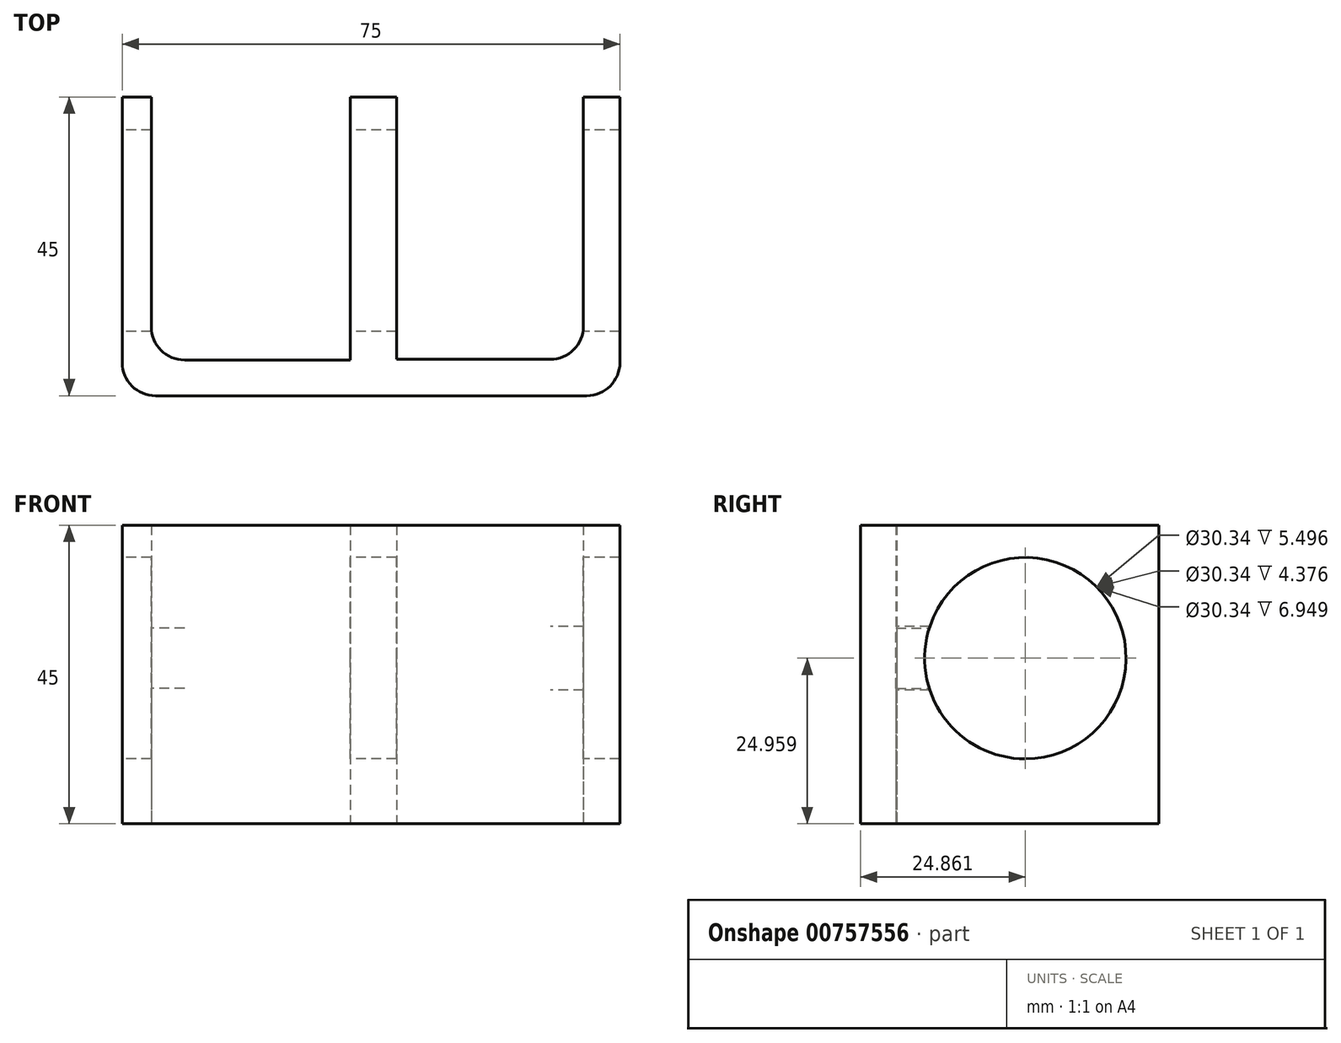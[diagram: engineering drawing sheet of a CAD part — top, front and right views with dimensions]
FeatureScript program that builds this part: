
annotation { "Feature Type Name" : "Feature", "Feature Type Description" : "" }
export const myFeature = defineFeature(function(context is Context, id is Id, definition is map)
    precondition{}
    {
        {
            var Q0;
            Q0=qCreatedBy(makeId("Top.planeOp"),FACE);
            var sketch = newSketch(context, id + "F0", { "sketchPlane" : qUnion([Q0])});
            skLineSegment(sketch, "E0.bottom", {"start": v(-37.5, 22.5) * mm, "end": v(37.5, 22.5) * mm});
            skLineSegment(sketch, "E0.top", {"start": v(-37.5, -22.5) * mm, "end": v(37.5, -22.5) * mm});
            skLineSegment(sketch, "E0.left", {"start": v(-37.5, 22.5) * mm, "end": v(-37.5, -22.5) * mm});
            skLineSegment(sketch, "E0.right", {"start": v(37.5, 22.5) * mm, "end": v(37.5, -22.5) * mm});
            skPoint(sketch, "E0.middle", {"position": v(0, 0) * mm});
            skLineSegment(sketch, "E1.bottom", {"start": v(-33.12, 24.35) * mm, "end": v(-3.12, 24.35) * mm});
            skLineSegment(sketch, "E1.top", {"start": v(-33.12, -17.11) * mm, "end": v(-3.12, -17.11) * mm});
            skLineSegment(sketch, "E1.left", {"start": v(-33.12, 24.35) * mm, "end": v(-33.12, -17.11) * mm});
            skLineSegment(sketch, "E1.right", {"start": v(-3.12, 24.35) * mm, "end": v(-3.12, -17.11) * mm});
            skLineSegment(sketch, "E2.bottom", {"start": v(3.83, 24.91) * mm, "end": v(32, 24.91) * mm});
            skLineSegment(sketch, "E2.top", {"start": v(3.83, -17.03) * mm, "end": v(32, -17.03) * mm});
            skLineSegment(sketch, "E2.left", {"start": v(3.83, 24.91) * mm, "end": v(3.83, -17.03) * mm});
            skLineSegment(sketch, "E2.right", {"start": v(32, 24.91) * mm, "end": v(32, -17.03) * mm});
            skSolve(sketch);
        }
        {
            var Q0;
            Q0=makeQuery(id+"F0.imprint","IMPRINT",FACE,{"disambiguationData":[TD([[makeQuery(id+"F0.imprint","IMPRINT",EDGE,{"derivedFrom":sQuery(id+"F0.wireOp",EDGE,"E0.top")}),1.0]])]});
            extrude(context, id + "F1", {"entities" : qUnion([Q0]), "depth" : 45 * mm, "offsetDistance" : 25 * mm});
        }
        {
            var Q0;
            Q0=makeQuery(id+"F1.opExtrude","SWEPT_EDGE",EDGE,{"disambiguationData":[OSD([sQuery(id+"F0.wireOp",EDGE,"E0.top"),sQuery(id+"F0.wireOp",EDGE,"E0.right")])]});
            var Q1;
            Q1=makeQuery(id+"F1.opExtrude","SWEPT_EDGE",EDGE,{"disambiguationData":[OSD([sQuery(id+"F0.wireOp",EDGE,"E0.top"),sQuery(id+"F0.wireOp",EDGE,"E0.left")])]});
            fillet(context, id + "F2", {"entities" : qUnion([Q0, Q1]), "radius" : 5 * mm, "tangentPropagation" : true, "allowEdgeOverflow" : false});
        }
        {
            var Q0;
            Q0=makeQuery(id+"F1.opExtrude","SWEPT_FACE",FACE,{"disambiguationData":[OSD([sQuery(id+"F0.wireOp",EDGE,"E0.left")])]});
            var sketch = newSketch(context, id + "F3", { "sketchPlane" : qUnion([Q0])});
            skCircle(sketch, "E3", {"center": v(-2.36, 24.96) * mm, "radius": 15.17 * mm});
            skPoint(sketch, "E3.first.point", {"position": v(-14.4, 34.19) * mm});
            skPoint(sketch, "E3.second.point", {"position": v(-10.1, 38) * mm});
            skPoint(sketch, "E3.third.point", {"position": v(-1.66, 40.11) * mm});
            skSolve(sketch);
        }
        {
            var Q0;
            Q0=makeQuery(id+"F3.imprint","IMPRINT",FACE,{"disambiguationData":[TD([[makeQuery(id+"F3.imprint","IMPRINT",EDGE,{"derivedFrom":sQuery(id+"F3.wireOp",EDGE,"E3")}),1.0]])]});
            extrude(context, id + "F4", {"entities" : qUnion([Q0]), "operationType" : NewBodyOperationType.REMOVE, "oppositeDirection" : true, "depth" : 100 * mm, "offsetDistance" : 25 * mm});
        }
        {
            var Q0;
            Q0=makeQuery(id+"F1.opExtrude","SWEPT_EDGE",EDGE,{"disambiguationData":[OSD([sQuery(id+"F0.wireOp",EDGE,"E1.top"),sQuery(id+"F0.wireOp",EDGE,"E1.left")])]});
            var Q1;
            Q1=makeQuery(id+"F1.opExtrude","SWEPT_EDGE",EDGE,{"disambiguationData":[OSD([sQuery(id+"F0.wireOp",EDGE,"E2.top"),sQuery(id+"F0.wireOp",EDGE,"E2.right")])]});
            fillet(context, id + "F5", {"entities" : qUnion([Q0, Q1]), "radius" : 5 * mm, "tangentPropagation" : true, "allowEdgeOverflow" : false});
        }
    });
